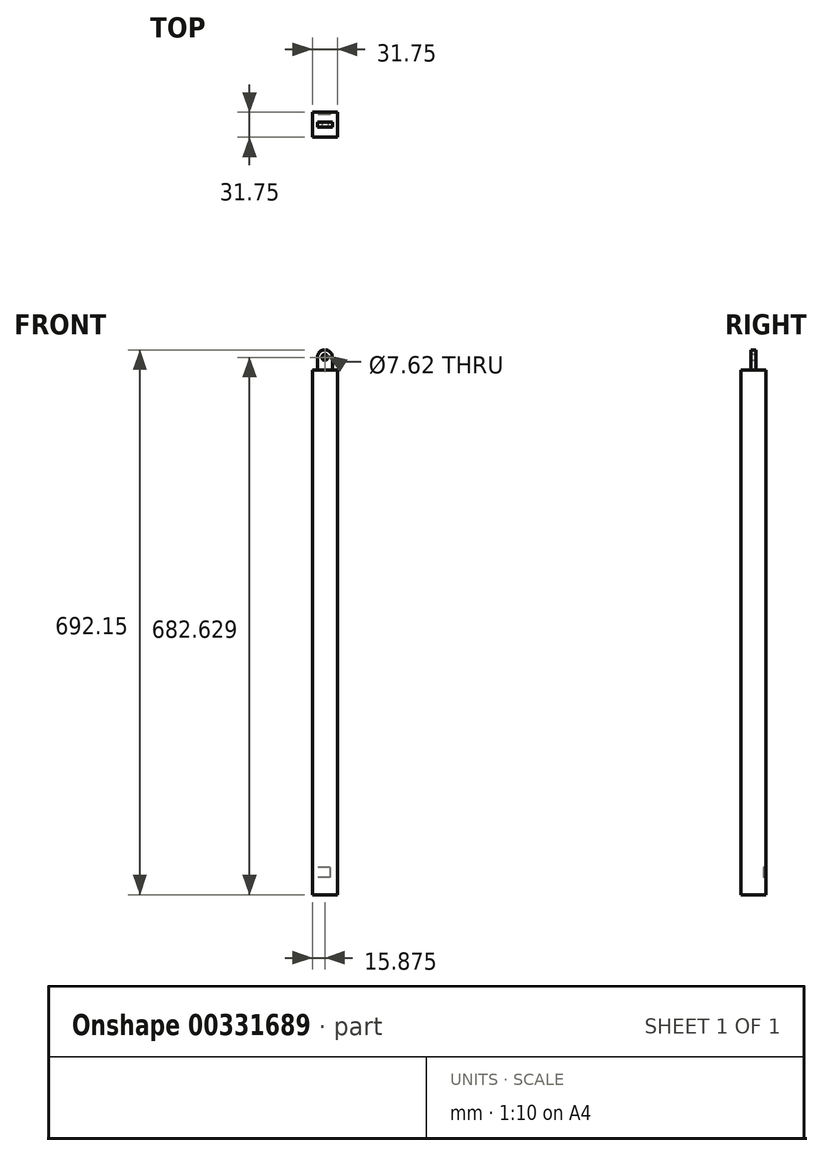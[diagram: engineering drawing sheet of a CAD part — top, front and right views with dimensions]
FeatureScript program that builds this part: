
annotation { "Feature Type Name" : "Feature", "Feature Type Description" : "" }
export const myFeature = defineFeature(function(context is Context, id is Id, definition is map)
    precondition{}
    {
        {
            var Q0;
            Q0=qCreatedBy(makeId("Front.planeOp"),FACE);
            var sketch = newSketch(context, id + "F0", { "sketchPlane" : qUnion([Q0])});
            skLineSegment(sketch, "E0.bottom", {"start": v(-31.75, 460.96) * mm, "end": v(0, 460.96) * mm});
            skLineSegment(sketch, "E0.top", {"start": v(-31.75, -205.79) * mm, "end": v(0, -205.79) * mm});
            skLineSegment(sketch, "E0.left", {"start": v(-31.75, 460.96) * mm, "end": v(-31.75, -205.79) * mm});
            skLineSegment(sketch, "E0.right", {"start": v(0, 460.96) * mm, "end": v(0, -205.79) * mm});
            skSolve(sketch);
        }
        {
            var Q0;
            Q0=makeQuery(id+"F0.imprint","IMPRINT",FACE,{"disambiguationData":[TD([[makeQuery(id+"F0.imprint","IMPRINT",EDGE,{"derivedFrom":sQuery(id+"F0.wireOp",EDGE,"E0.bottom")}),-1.0]])]});
            extrude(context, id + "F1", {"entities" : qUnion([Q0]), "oppositeDirection" : true, "depth" : 31.75 * mm});
        }
        {
            var Q0;
            Q0=makeQuery(id+"F1.opExtrude","SWEPT_FACE",FACE,{"disambiguationData":[OSD([sQuery(id+"F0.wireOp",EDGE,"E0.bottom")])]});
            var sketch = newSketch(context, id + "F2", { "sketchPlane" : qUnion([Q0])});
            skLineSegment(sketch, "E1.bottom", {"start": v(-25.4, 19.05) * mm, "end": v(-6.35, 19.05) * mm});
            skLineSegment(sketch, "E1.top", {"start": v(-25.4, 12.7) * mm, "end": v(-6.35, 12.7) * mm});
            skLineSegment(sketch, "E1.left", {"start": v(-25.4, 19.05) * mm, "end": v(-25.4, 12.7) * mm});
            skLineSegment(sketch, "E1.right", {"start": v(-6.35, 19.05) * mm, "end": v(-6.35, 12.7) * mm});
            skSolve(sketch);
        }
        {
            var Q0;
            Q0=makeQuery(id+"F2.imprint","IMPRINT",FACE,{"disambiguationData":[TD([[makeQuery(id+"F2.imprint","IMPRINT",EDGE,{"derivedFrom":sQuery(id+"F2.wireOp",EDGE,"E1.bottom")}),-1.0]])]});
            extrude(context, id + "F3", {"entities" : qUnion([Q0]), "operationType" : NewBodyOperationType.ADD, "depth" : 25.4 * mm});
        }
        {
            var Q0;
            Q0=makeQuery(id+"F3.opExtrude","CAP_EDGE",EDGE,{"disambiguationData":[OSD([sQuery(id+"F2.wireOp",EDGE,"E1.right")])],"isStart":false});
            var Q1;
            Q1=makeQuery(id+"F3.opExtrude","CAP_EDGE",EDGE,{"disambiguationData":[OSD([sQuery(id+"F2.wireOp",EDGE,"E1.left")])],"isStart":false});
            fillet(context, id + "F4", {"entities" : qUnion([Q0, Q1]), "radius" : 9.52 * mm, "tangentPropagation" : true, "allowEdgeOverflow" : false});
        }
        {
            var Q0;
            Q0=makeQuery(id+"F3.opExtrude","SWEPT_FACE",FACE,{"disambiguationData":[OSD([sQuery(id+"F2.wireOp",EDGE,"E1.top")])]});
            var sketch = newSketch(context, id + "F5", { "sketchPlane" : qUnion([Q0])});
            skCircle(sketch, "E2", {"center": v(-15.88, 476.84) * mm, "radius": 3.81 * mm});
            skSolve(sketch);
        }
        {
            var Q0;
            Q0 = qSketchRegion(id + "F5", true);
            extrude(context, id + "F6", {"entities" : qUnion([Q0]), "operationType" : NewBodyOperationType.REMOVE, "oppositeDirection" : true, "depth" : 6.35 * mm});
        }
        {
            var Q0;
            Q0=makeQuery(id+"F1.opExtrude","SWEPT_FACE",FACE,{"disambiguationData":[OSD([sQuery(id+"F0.wireOp",EDGE,"E0.left")])]});
            var sketch = newSketch(context, id + "F7", { "sketchPlane" : qUnion([Q0])});
            skLineSegment(sketch, "E3.bottom", {"start": v(-30.16, -170.86) * mm, "end": v(-28.58, -170.86) * mm});
            skLineSegment(sketch, "E3.top", {"start": v(-30.16, -183.56) * mm, "end": v(-28.58, -183.56) * mm});
            skLineSegment(sketch, "E3.left", {"start": v(-30.16, -170.86) * mm, "end": v(-30.16, -183.56) * mm});
            skLineSegment(sketch, "E3.right", {"start": v(-28.58, -170.86) * mm, "end": v(-28.58, -183.56) * mm});
            skSolve(sketch);
        }
        {
            var Q0;
            Q0 = qSketchRegion(id + "F7", true);
            extrude(context, id + "F8", {"entities" : qUnion([Q0]), "operationType" : NewBodyOperationType.REMOVE, "oppositeDirection" : true, "depth" : 22.22 * mm});
        }
    });
